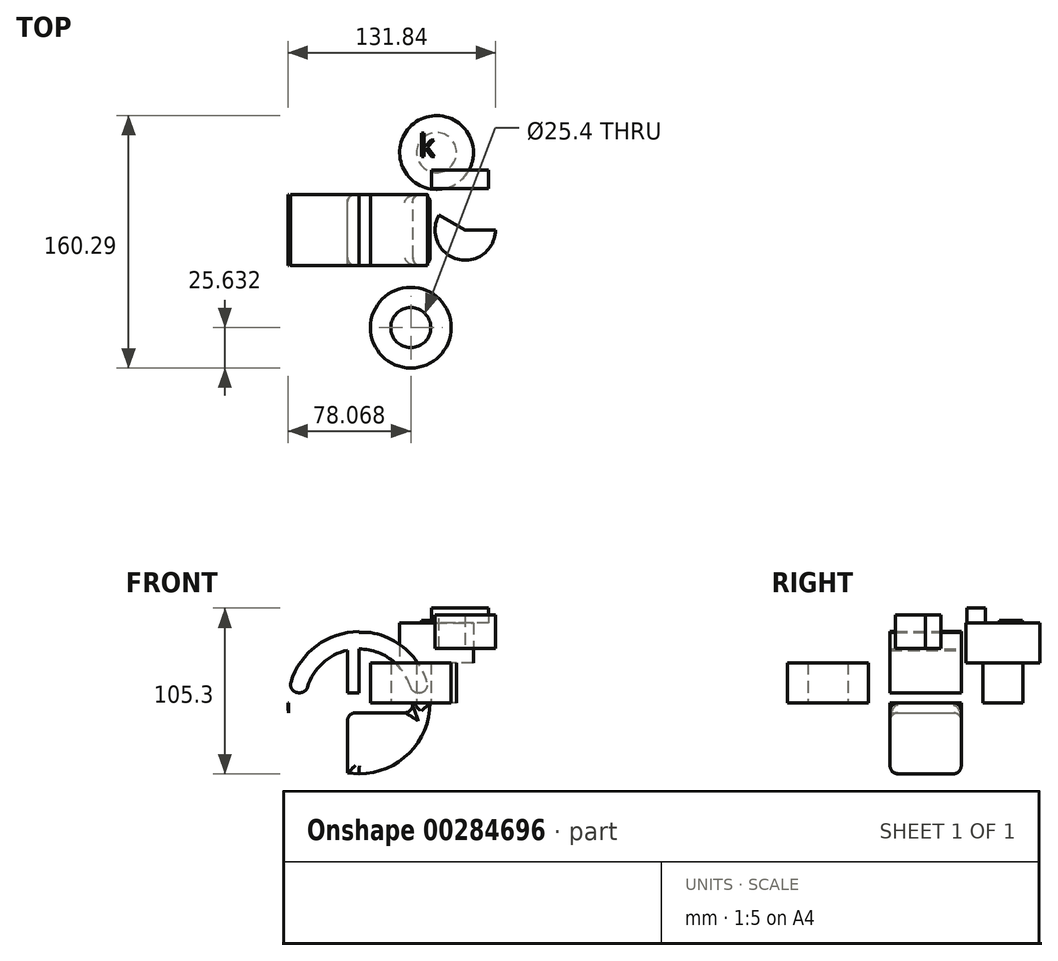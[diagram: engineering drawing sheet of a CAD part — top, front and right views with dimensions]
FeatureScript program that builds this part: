
annotation { "Feature Type Name" : "Feature", "Feature Type Description" : "" }
export const myFeature = defineFeature(function(context is Context, id is Id, definition is map)
    precondition{}
    {
        {
            var Q0;
            Q0=qCreatedBy(makeId("Front.planeOp"),FACE);
            var sketch = newSketch(context, id + "F0", { "sketchPlane" : qUnion([Q0])});
            skCircle(sketch, "E0", {"center": v(0, 0) * mm, "radius": 45.17 * mm});
            skCircle(sketch, "E1", {"center": v(0, 0) * mm, "radius": 34.15 * mm});
            skLineSegment(sketch, "E2", {"start": v(0, 0) * mm, "end": v(45.17, 0) * mm});
            skLineSegment(sketch, "E3", {"start": v(45.17, 0) * mm, "end": v(-45.17, 0) * mm});
            skLineSegment(sketch, "E4", {"start": v(-45.17, 0) * mm, "end": v(0, 0) * mm});
            skLineSegment(sketch, "E5", {"start": v(0, 45.17) * mm, "end": v(0, -45.17) * mm});
            skLineSegment(sketch, "E6", {"start": v(0, -45.17) * mm, "end": v(-7.33, -44.57) * mm});
            skLineSegment(sketch, "E7", {"start": v(-7.33, -44.57) * mm, "end": v(-7.33, 44.57) * mm});
            skLineSegment(sketch, "E8", {"start": v(-7.33, 44.57) * mm, "end": v(7.33, 44.57) * mm});
            skLineSegment(sketch, "E9", {"start": v(7.33, 44.57) * mm, "end": v(7.33, -45.17) * mm});
            skLineSegment(sketch, "E10", {"start": v(7.33, -45.17) * mm, "end": v(7.33, 0) * mm});
            skLineSegment(sketch, "E11", {"start": v(7.33, 0) * mm, "end": v(45.17, 0) * mm});
            skLineSegment(sketch, "E12", {"start": v(44.72, 6.38) * mm, "end": v(-44.72, 6.38) * mm});
            skLineSegment(sketch, "E13", {"start": v(-44.72, 6.38) * mm, "end": v(-44.72, -6.38) * mm});
            skLineSegment(sketch, "E14", {"start": v(-44.72, -6.38) * mm, "end": v(45.17, -6.38) * mm});
            skSolve(sketch);
        }
        {
            var Q0;
            {var subQ0=sQuery(id+"F0.wireOp",EDGE,"E7");var subQ5=sQuery(id+"F0.wireOp",EDGE,"E1");var subQ6=makeQuery(id+"F0.imprint","INTERSECT",VERTEX,{"disambiguationData":[OD(0.0)],"derivedFrom":[subQ5,subQ0]});Q0=makeQuery(id+"F0.imprint","IMPRINT",FACE,{"disambiguationData":[TD([[makeQuery(id+"F0.imprint","IMPRINT",EDGE,{"disambiguationData":[TD([[subQ6,-1.0]])],"derivedFrom":subQ5}),-1.0]])]});}
            var Q1;
            {var subQ0=sQuery(id+"F0.wireOp",EDGE,"E5");var subQ1=sQuery(id+"F0.wireOp",EDGE,"E1");var subQ2=makeQuery(id+"F0.imprint","INTERSECT",VERTEX,{"disambiguationData":[OD(0.0)],"derivedFrom":[subQ1,subQ0]});Q1=makeQuery(id+"F0.imprint","IMPRINT",FACE,{"disambiguationData":[TD([[makeQuery(id+"F0.imprint","IMPRINT",EDGE,{"disambiguationData":[TD([[subQ2,-1.0]])],"derivedFrom":subQ1}),1.0]])]});}
            var Q2;
            {var subQ0=sQuery(id+"F0.wireOp",EDGE,"E9");var subQ1=sQuery(id+"F0.wireOp",EDGE,"E1");var subQ2=makeQuery(id+"F0.imprint","INTERSECT",VERTEX,{"derivedFrom":[subQ1,subQ0]});Q2=makeQuery(id+"F0.imprint","IMPRINT",FACE,{"disambiguationData":[TD([[makeQuery(id+"F0.imprint","IMPRINT",EDGE,{"disambiguationData":[TD([[subQ2,-1.0]])],"derivedFrom":subQ1}),1.0]])]});}
            var Q3;
            {var subQ0=sQuery(id+"F0.wireOp",EDGE,"E5");var subQ1=sQuery(id+"F0.wireOp",EDGE,"E1");var subQ2=makeQuery(id+"F0.imprint","INTERSECT",VERTEX,{"disambiguationData":[OD(0.0)],"derivedFrom":[subQ1,subQ0]});Q3=makeQuery(id+"F0.imprint","IMPRINT",FACE,{"disambiguationData":[TD([[makeQuery(id+"F0.imprint","IMPRINT",EDGE,{"disambiguationData":[TD([[subQ2,-1.0]])],"derivedFrom":subQ1}),-1.0]])]});}
            var Q4;
            {var subQ0=sQuery(id+"F0.wireOp",EDGE,"E9");var subQ1=sQuery(id+"F0.wireOp",EDGE,"E1");var subQ2=makeQuery(id+"F0.imprint","INTERSECT",VERTEX,{"derivedFrom":[subQ1,subQ0]});Q4=makeQuery(id+"F0.imprint","IMPRINT",FACE,{"disambiguationData":[TD([[makeQuery(id+"F0.imprint","IMPRINT",EDGE,{"disambiguationData":[TD([[subQ2,-1.0]])],"derivedFrom":subQ1}),-1.0]])]});}
            var Q5;
            {var subQ3=sQuery(id+"F0.wireOp",EDGE,"E12");var subQ5=sQuery(id+"F0.wireOp",EDGE,"E1");var subQ6=makeQuery(id+"F0.imprint","INTERSECT",VERTEX,{"disambiguationData":[OD(0.0)],"derivedFrom":[subQ5,subQ3]});Q5=makeQuery(id+"F0.imprint","IMPRINT",FACE,{"disambiguationData":[TD([[makeQuery(id+"F0.imprint","IMPRINT",EDGE,{"disambiguationData":[TD([[subQ6,-1.0]])],"derivedFrom":subQ5}),-1.0]])]});}
            var Q6;
            {var subQ5=sQuery(id+"F0.wireOp",EDGE,"E6");Q6=makeQuery(id+"F0.imprint","IMPRINT",FACE,{"disambiguationData":[TD([[makeQuery(id+"F0.imprint","IMPRINT",EDGE,{"derivedFrom":subQ5}),-1.0]])]});}
            var Q7;
            {var subQ0=sQuery(id+"F0.wireOp",EDGE,"E5");var subQ5=sQuery(id+"F0.wireOp",EDGE,"E1");var subQ6=makeQuery(id+"F0.imprint","INTERSECT",VERTEX,{"disambiguationData":[OD(1.0)],"derivedFrom":[subQ5,subQ0]});Q7=makeQuery(id+"F0.imprint","IMPRINT",FACE,{"disambiguationData":[TD([[makeQuery(id+"F0.imprint","IMPRINT",EDGE,{"disambiguationData":[TD([[subQ6,-1.0]])],"derivedFrom":subQ5}),-1.0]])]});}
            var Q8;
            {var subQ3=sQuery(id+"F0.wireOp",EDGE,"E14");var subQ5=sQuery(id+"F0.wireOp",EDGE,"E1");var subQ7=makeQuery(id+"F0.imprint","INTERSECT",VERTEX,{"disambiguationData":[OD(0.0)],"derivedFrom":[subQ5,subQ3]});Q8=makeQuery(id+"F0.imprint","IMPRINT",FACE,{"disambiguationData":[TD([[makeQuery(id+"F0.imprint","IMPRINT",EDGE,{"disambiguationData":[TD([[subQ7,-1.0]])],"derivedFrom":subQ5}),-1.0]])]});}
            var Q9;
            {var subQ0=sQuery(id+"F0.wireOp",EDGE,"E7");var subQ1=sQuery(id+"F0.wireOp",EDGE,"E1");var subQ2=makeQuery(id+"F0.imprint","INTERSECT",VERTEX,{"disambiguationData":[OD(1.0)],"derivedFrom":[subQ1,subQ0]});Q9=makeQuery(id+"F0.imprint","IMPRINT",FACE,{"disambiguationData":[TD([[makeQuery(id+"F0.imprint","IMPRINT",EDGE,{"disambiguationData":[TD([[subQ2,-1.0]])],"derivedFrom":subQ1}),1.0]])]});}
            var Q10;
            {var subQ0=sQuery(id+"F0.wireOp",EDGE,"E5");var subQ1=sQuery(id+"F0.wireOp",EDGE,"E1");var subQ2=makeQuery(id+"F0.imprint","INTERSECT",VERTEX,{"disambiguationData":[OD(1.0)],"derivedFrom":[subQ1,subQ0]});Q10=makeQuery(id+"F0.imprint","IMPRINT",FACE,{"disambiguationData":[TD([[makeQuery(id+"F0.imprint","IMPRINT",EDGE,{"disambiguationData":[TD([[subQ2,-1.0]])],"derivedFrom":subQ1}),1.0]])]});}
            var Q11;
            {var subQ0=sQuery(id+"F0.wireOp",EDGE,"E10");var subQ1=sQuery(id+"F0.wireOp",EDGE,"E0");var subQ2=makeQuery(id+"F0.imprint","INTERSECT",VERTEX,{"derivedFrom":[subQ1,subQ0]});Q11=makeQuery(id+"F0.imprint","IMPRINT",FACE,{"disambiguationData":[TD([[makeQuery(id+"F0.imprint","IMPRINT",EDGE,{"disambiguationData":[TD([[subQ2,-1.0]])],"derivedFrom":subQ1}),1.0]])]});}
            extrude(context, id + "F1", {"entities" : qUnion([Q0, Q1, Q2, Q3, Q4, Q5, Q6, Q7, Q8, Q9, Q10, Q11]), "endBound" : BoundingType.SYMMETRIC, "depth" : 45.2 * mm});
        }
        {
            var Q0;
            {var subQ0=sQuery(id+"F0.wireOp",EDGE,"E0");Q0=makeQuery(id+"F1.opExtrude","CAP_EDGE",EDGE,{"disambiguationData":[OSD([subQ0]),TDD([makeQuery(id+"F0.imprint","IMPRINT",EDGE,{"disambiguationData":[TD([[makeQuery(id+"F0.imprint","INTERSECT",VERTEX,{"derivedFrom":[subQ0,sQuery(id+"F0.wireOp",EDGE,"E12")]}),-1.0]])],"derivedFrom":subQ0})])],"isStart":false});}
            var Q1;
            {var subQ0=sQuery(id+"F0.wireOp",EDGE,"E0");Q1=makeQuery(id+"F1.opExtrude","CAP_EDGE",EDGE,{"disambiguationData":[OSD([subQ0]),TDD([makeQuery(id+"F0.imprint","IMPRINT",EDGE,{"disambiguationData":[TD([[makeQuery(id+"F0.imprint","INTERSECT",VERTEX,{"derivedFrom":[subQ0,sQuery(id+"F0.wireOp",EDGE,"E12")]}),-1.0]])],"derivedFrom":subQ0})])],"isStart":true});}
            var Q2;
            Q2=makeQuery(id+"F1.opExtrude","SWEPT_EDGE",EDGE,{"disambiguationData":[OSD([sQuery(id+"F0.wireOp",EDGE,"E7"),sQuery(id+"F0.wireOp",EDGE,"E12")])]});
            var Q3;
            Q3=makeQuery(id+"F1.opExtrude","SWEPT_EDGE",EDGE,{"disambiguationData":[OSD([sQuery(id+"F0.wireOp",EDGE,"E9"),sQuery(id+"F0.wireOp",EDGE,"E12")])]});
            var Q4;
            Q4=makeQuery(id+"F1.opExtrude","CAP_FACE",FACE,{"disambiguationData":[OSD([sQuery(id+"F0.wireOp",EDGE,"E0"),sQuery(id+"F0.wireOp",EDGE,"E1"),sQuery(id+"F0.wireOp",EDGE,"E7"),sQuery(id+"F0.wireOp",EDGE,"E8"),sQuery(id+"F0.wireOp",EDGE,"E9"),sQuery(id+"F0.wireOp",EDGE,"E12")])],"isStart":true});
            var Q5;
            Q5=makeQuery(id+"F1.opExtrude","CAP_FACE",FACE,{"disambiguationData":[OSD([sQuery(id+"F0.wireOp",EDGE,"E0"),sQuery(id+"F0.wireOp",EDGE,"E1"),sQuery(id+"F0.wireOp",EDGE,"E7"),sQuery(id+"F0.wireOp",EDGE,"E8"),sQuery(id+"F0.wireOp",EDGE,"E9"),sQuery(id+"F0.wireOp",EDGE,"E12")])],"isStart":false});
            var Q6;
            Q6=makeQuery(id+"F1.opExtrude","CAP_FACE",FACE,{"disambiguationData":[OSD([sQuery(id+"F0.wireOp",EDGE,"E0"),sQuery(id+"F0.wireOp",EDGE,"E1"),sQuery(id+"F0.wireOp",EDGE,"E6"),sQuery(id+"F0.wireOp",EDGE,"E7"),sQuery(id+"F0.wireOp",EDGE,"E10"),sQuery(id+"F0.wireOp",EDGE,"E14")])],"isStart":true});
            var Q7;
            Q7=makeQuery(id+"F1.opExtrude","CAP_FACE",FACE,{"disambiguationData":[OSD([sQuery(id+"F0.wireOp",EDGE,"E0"),sQuery(id+"F0.wireOp",EDGE,"E1"),sQuery(id+"F0.wireOp",EDGE,"E6"),sQuery(id+"F0.wireOp",EDGE,"E7"),sQuery(id+"F0.wireOp",EDGE,"E10"),sQuery(id+"F0.wireOp",EDGE,"E14")])],"isStart":false});
            fillet(context, id + "F2", {"entities" : qUnion([Q0, Q1, Q2, Q3, Q4, Q5, Q6, Q7]), "radius" : 5.08 * mm, "tangentPropagation" : true, "allowEdgeOverflow" : false});
        }
        {
            var Q0;
            Q0=makeQuery(id+"F1.opExtrude","SWEPT_EDGE",EDGE,{"disambiguationData":[OSD([sQuery(id+"F0.wireOp",EDGE,"E0"),sQuery(id+"F0.wireOp",EDGE,"E14")])]});
            var Q1;
            Q1=makeQuery(id+"F1.opExtrude","SWEPT_EDGE",EDGE,{"disambiguationData":[OSD([sQuery(id+"F0.wireOp",EDGE,"E0"),sQuery(id+"F0.wireOp",EDGE,"E12")])]});
            var Q2;
            {var subQ0=sQuery(id+"F0.wireOp",EDGE,"E14");var subQ1=sQuery(id+"F0.wireOp",EDGE,"E1");Q2=makeQuery(id+"F1.opExtrude","SWEPT_EDGE",EDGE,{"disambiguationData":[OSD([subQ1,subQ0]),TDD([makeQuery(id+"F0.imprint","INTERSECT",VERTEX,{"disambiguationData":[OD(1.0)],"derivedFrom":[subQ1,subQ0]})])]});}
            var Q3;
            {var subQ0=sQuery(id+"F0.wireOp",EDGE,"E12");var subQ1=sQuery(id+"F0.wireOp",EDGE,"E1");Q3=makeQuery(id+"F1.opExtrude","SWEPT_EDGE",EDGE,{"disambiguationData":[OSD([subQ1,subQ0]),TDD([makeQuery(id+"F0.imprint","INTERSECT",VERTEX,{"disambiguationData":[OD(0.0)],"derivedFrom":[subQ1,subQ0]})])]});}
            var Q4;
            Q4=makeQuery(id+"F1.opExtrude","SWEPT_EDGE",EDGE,{"disambiguationData":[OSD([sQuery(id+"F0.wireOp",EDGE,"E7"),sQuery(id+"F0.wireOp",EDGE,"E14")])]});
            var Q5;
            Q5=makeQuery(id+"F1.opExtrude","SWEPT_EDGE",EDGE,{"disambiguationData":[OSD([sQuery(id+"F0.wireOp",EDGE,"E10"),sQuery(id+"F0.wireOp",EDGE,"E14")])]});
            var Q6;
            Q6=makeQuery(id+"F1.opExtrude","SWEPT_EDGE",EDGE,{"disambiguationData":[OSD([sQuery(id+"F0.wireOp",EDGE,"E0"),sQuery(id+"F0.wireOp",EDGE,"E13"),sQuery(id+"F0.wireOp",EDGE,"E14")])]});
            var Q7;
            {var subQ0=sQuery(id+"F0.wireOp",EDGE,"E14");var subQ1=sQuery(id+"F0.wireOp",EDGE,"E1");Q7=makeQuery(id+"F1.opExtrude","SWEPT_EDGE",EDGE,{"disambiguationData":[OSD([subQ1,subQ0]),TDD([makeQuery(id+"F0.imprint","INTERSECT",VERTEX,{"disambiguationData":[OD(0.0)],"derivedFrom":[subQ1,subQ0]})])]});}
            var Q8;
            Q8=makeQuery(id+"F1.opExtrude","SWEPT_EDGE",EDGE,{"disambiguationData":[OSD([sQuery(id+"F0.wireOp",EDGE,"E0"),sQuery(id+"F0.wireOp",EDGE,"E12"),sQuery(id+"F0.wireOp",EDGE,"E13")])]});
            var Q9;
            {var subQ0=sQuery(id+"F0.wireOp",EDGE,"E12");var subQ1=sQuery(id+"F0.wireOp",EDGE,"E1");Q9=makeQuery(id+"F1.opExtrude","SWEPT_EDGE",EDGE,{"disambiguationData":[OSD([subQ1,subQ0]),TDD([makeQuery(id+"F0.imprint","INTERSECT",VERTEX,{"disambiguationData":[OD(1.0)],"derivedFrom":[subQ1,subQ0]})])]});}
            fillet(context, id + "F3", {"entities" : qUnion([Q0, Q1, Q2, Q3, Q4, Q5, Q6, Q7, Q8, Q9]), "radius" : 5.08 * mm, "tangentPropagation" : true, "allowEdgeOverflow" : false});
        }
        {
            var Q0;
            Q0=qCreatedBy(makeId("Front.planeOp"),FACE);
            var sketch = newSketch(context, id + "F4", { "sketchPlane" : qUnion([Q0])});
            skLineSegment(sketch, "E15.bottom", {"start": v(48.28, 34.5) * mm, "end": v(86.67, 34.5) * mm});
            skLineSegment(sketch, "E15.top", {"start": v(48.28, 55.78) * mm, "end": v(86.67, 55.78) * mm});
            skLineSegment(sketch, "E15.left", {"start": v(48.28, 34.5) * mm, "end": v(48.28, 55.78) * mm});
            skLineSegment(sketch, "E15.right", {"start": v(86.67, 34.5) * mm, "end": v(86.67, 55.78) * mm});
            skPoint(sketch, "E15.middle", {"position": v(67.48, 45.14) * mm});
            skLineSegment(sketch, "E16", {"start": v(67.48, 45.14) * mm, "end": v(67.48, 34.5) * mm});
            skLineSegment(sketch, "E17", {"start": v(67.48, 34.5) * mm, "end": v(67.48, 55.78) * mm});
            skSolve(sketch);
        }
        {
            var Q0;
            {var subQ0=sQuery(id+"F4.wireOp",EDGE,"E15.right");Q0=makeQuery(id+"F4.imprint","IMPRINT",FACE,{"disambiguationData":[TD([[makeQuery(id+"F4.imprint","IMPRINT",EDGE,{"derivedFrom":subQ0}),1.0]])]});}
            var Q1;
            Q1=sQuery(id+"F4.wireOp",EDGE,"E17");
            revolve(context, id + "F5", {"entities" : qUnion([Q0]), "axis" : qUnion([Q1]), "revolveType" : RevolveType.ONE_DIRECTION, "oppositeDirection" : true, "angle" : 210 * degree});
        }
        {
            var Q0;
            Q0=qCreatedBy(makeId("Top.planeOp"),FACE);
            var sketch = newSketch(context, id + "F6", { "sketchPlane" : qUnion([Q0])});
            skCircle(sketch, "E18", {"center": v(49.26, 49.16) * mm, "radius": 12.7 * mm});
            skSolve(sketch);
        }
        {
            var Q0;
            Q0=makeQuery(id+"F6.imprint","IMPRINT",FACE,{"disambiguationData":[TD([[makeQuery(id+"F6.imprint","IMPRINT",EDGE,{"derivedFrom":sQuery(id+"F6.wireOp",EDGE,"E18")}),1.0]])]});
            extrude(context, id + "F7", {"entities" : qUnion([Q0]), "depth" : 25.4 * mm});
        }
        {
            var Q0;
            Q0=qCreatedBy(makeId("Top.planeOp"),FACE);
            var sketch = newSketch(context, id + "F8", { "sketchPlane" : qUnion([Q0])});
            skCircle(sketch, "E19", {"center": v(32.9, -62.08) * mm, "radius": 12.7 * mm});
            skCircle(sketch, "E20", {"center": v(32.9, -62.08) * mm, "radius": 25.63 * mm});
            skSolve(sketch);
        }
        {
            var Q0;
            Q0=makeQuery(id+"F8.imprint","IMPRINT",FACE,{"disambiguationData":[TD([[makeQuery(id+"F8.imprint","IMPRINT",EDGE,{"derivedFrom":sQuery(id+"F8.wireOp",EDGE,"E19")}),-1.0]])]});
            extrude(context, id + "F9", {"entities" : qUnion([Q0]), "depth" : 25.4 * mm});
        }
        {
            var Q0;
            Q0=makeQuery(id+"F7.opExtrude","CAP_FACE",FACE,{"disambiguationData":[OSD([sQuery(id+"F6.wireOp",EDGE,"E18")])],"isStart":false});
            var sketch = newSketch(context, id + "F10", { "sketchPlane" : qUnion([Q0])});
            skCircle(sketch, "E21", {"center": v(49.26, 49.16) * mm, "radius": 23.42 * mm});
            skSolve(sketch);
        }
        {
            var Q0;
            Q0 = qSketchRegion(id + "F10", true);
            extrude(context, id + "F11", {"entities" : qUnion([Q0]), "operationType" : NewBodyOperationType.ADD, "depth" : 25.4 * mm});
        }
        {
            var Q0;
            Q0=qCreatedBy(makeId("Right.planeOp"),FACE);
            cPlane(context, id + "F12", {"entities" : qUnion([Q0]), "cplaneType" : CPlaneType.OFFSET, "offset" : 45.97 * mm, "width" : 152.4 * mm, "height" : 152.4 * mm});
        }
        {
            var Q0;
            Q0=qCreatedBy(id+"F12.planeOp",FACE);
            var sketch = newSketch(context, id + "F13", { "sketchPlane" : qUnion([Q0])});
            skLineSegment(sketch, "E22.bottom", {"start": v(38.07, 60.13) * mm, "end": v(26.34, 60.13) * mm});
            skLineSegment(sketch, "E22.top", {"start": v(38.07, 50.82) * mm, "end": v(26.34, 50.82) * mm});
            skLineSegment(sketch, "E22.left", {"start": v(38.07, 60.13) * mm, "end": v(38.07, 50.82) * mm});
            skLineSegment(sketch, "E22.right", {"start": v(26.34, 60.13) * mm, "end": v(26.34, 50.82) * mm});
            skPoint(sketch, "E22.middle", {"position": v(32.2, 55.48) * mm});
            skSolve(sketch);
        }
        {
            var Q0;
            Q0=makeQuery(id+"F13.imprint","IMPRINT",FACE,{"disambiguationData":[TD([[makeQuery(id+"F13.imprint","IMPRINT",EDGE,{"derivedFrom":sQuery(id+"F13.wireOp",EDGE,"E22.bottom")}),1.0]])]});
            extrude(context, id + "F14", {"entities" : qUnion([Q0]), "depth" : 36.32 * mm});
        }
        {
            var Q0;
            Q0=makeQuery(id+"F11.opExtrude","CAP_FACE",FACE,{"disambiguationData":[OSD([sQuery(id+"F10.wireOp",EDGE,"E21")])],"isStart":false});
            var sketch = newSketch(context, id + "F15", { "sketchPlane" : qUnion([Q0])});
            skText(sketch, "E23", { "text": "k", "fontName": "OpenSans-Regular.ttf"});
            const initialGuessF15  = {"E23": [0.03794, 0.04673, 1, 0, 0.01411]};
            skSetInitialGuess(sketch, initialGuessF15);
            skSolve(sketch);
        }
        {
            var Q0;
            Q0 = qSketchRegion(id + "F15", true);
            extrude(context, id + "F16", {"entities" : qUnion([Q0]), "operationType" : NewBodyOperationType.ADD, "depth" : 1.52 * mm});
        }
    });
